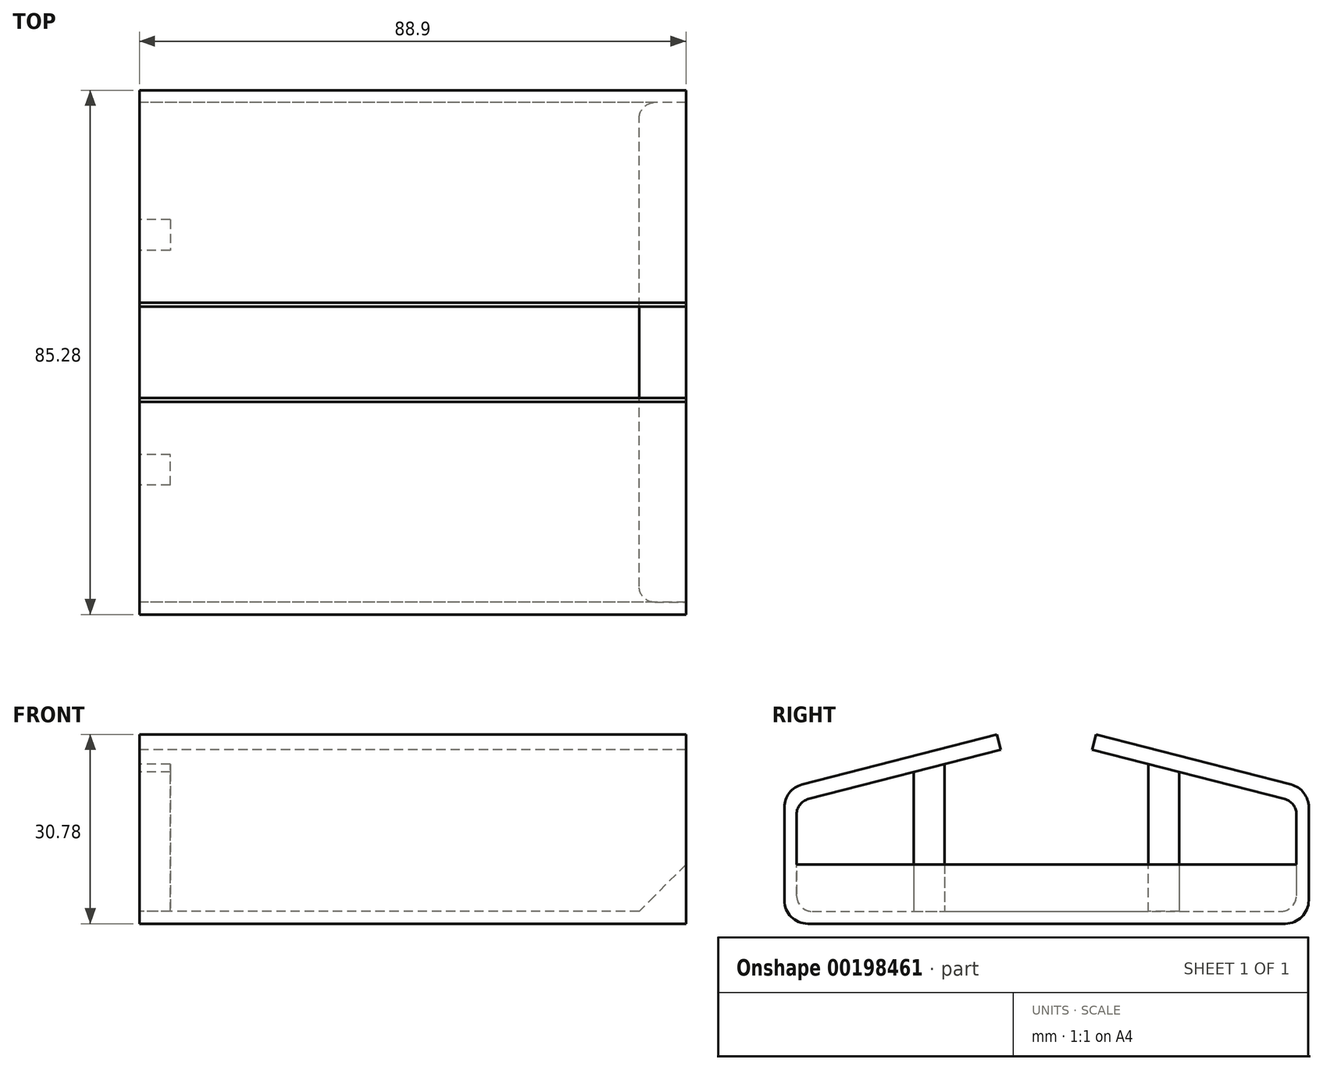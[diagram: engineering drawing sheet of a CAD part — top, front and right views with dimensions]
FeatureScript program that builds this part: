
annotation { "Feature Type Name" : "Feature", "Feature Type Description" : "" }
export const myFeature = defineFeature(function(context is Context, id is Id, definition is map)
    precondition{}
    {
        {
            var Q0;
            Q0=qCreatedBy(makeId("Right.planeOp"),FACE);
            var sketch = newSketch(context, id + "F0", { "sketchPlane" : qUnion([Q0])});
            skLineSegment(sketch, "E0.top", {"start": v(-25.4, 0) * mm, "end": v(59.88, 0) * mm});
            skLineSegment(sketch, "E0.left", {"start": v(-25.4, 21.89) * mm, "end": v(-25.4, 0) * mm});
            skLineSegment(sketch, "E0.right", {"start": v(59.88, 21.89) * mm, "end": v(59.88, 0) * mm});
            skLineSegment(sketch, "E1.top", {"start": v(-23.4, 2) * mm, "end": v(57.88, 2) * mm});
            skLineSegment(sketch, "E1.left", {"start": v(-23.4, 19.78) * mm, "end": v(-23.4, 2) * mm});
            skLineSegment(sketch, "E1.right", {"start": v(57.88, 19.78) * mm, "end": v(57.88, 2) * mm});
            skLineSegment(sketch, "E2", {"start": v(59.88, 21.89) * mm, "end": v(25.3, 30.78) * mm});
            skLineSegment(sketch, "E3", {"start": v(25.3, 30.78) * mm, "end": v(24.67, 28.32) * mm});
            skLineSegment(sketch, "E4", {"start": v(24.67, 28.32) * mm, "end": v(57.88, 19.78) * mm});
            skLineSegment(sketch, "E5", {"start": v(17.24, 0) * mm, "end": v(17.24, 27.47) * mm});
            skLineSegment(sketch, "E6.MirrorCS", {"start": v(9.8, 28.32) * mm, "end": v(-23.4, 19.78) * mm});
            skLineSegment(sketch, "E7.MirrorCS", {"start": v(-25.4, 21.89) * mm, "end": v(9.18, 30.78) * mm});
            skLineSegment(sketch, "E8.MirrorCS", {"start": v(9.18, 30.78) * mm, "end": v(9.8, 28.32) * mm});
            skSolve(sketch);
        }
        {
            var Q0;
            {var subQ4=sQuery(id+"F0.wireOp",EDGE,"E0.right");Q0=makeQuery(id+"F0.imprint","IMPRINT",FACE,{"disambiguationData":[TD([[makeQuery(id+"F0.imprint","IMPRINT",EDGE,{"derivedFrom":subQ4}),-1.0]])]});}
            var Q1;
            {var subQ4=sQuery(id+"F0.wireOp",EDGE,"E0.left");Q1=makeQuery(id+"F0.imprint","IMPRINT",FACE,{"disambiguationData":[TD([[makeQuery(id+"F0.imprint","IMPRINT",EDGE,{"derivedFrom":subQ4}),1.0]])]});}
            extrude(context, id + "F1", {"entities" : qUnion([Q0, Q1]), "depth" : 88.9 * mm});
        }
        {
            var Q0;
            Q0=qCreatedBy(makeId("Right.planeOp"),FACE);
            var sketch = newSketch(context, id + "F2", { "sketchPlane" : qUnion([Q0])});
            skLineSegment(sketch, "E9.top", {"start": v(38.83, 2) * mm, "end": v(33.83, 2) * mm});
            skLineSegment(sketch, "E9.left", {"start": v(38.83, 17.7) * mm, "end": v(38.83, 2) * mm});
            skLineSegment(sketch, "E9.right", {"start": v(33.83, 17.7) * mm, "end": v(33.83, 2) * mm});
            skLineSegment(sketch, "E10.top", {"start": v(-4.35, 2) * mm, "end": v(0.65, 2) * mm});
            skLineSegment(sketch, "E10.left", {"start": v(-4.35, 17.7) * mm, "end": v(-4.35, 2) * mm});
            skLineSegment(sketch, "E10.right", {"start": v(0.65, 17.7) * mm, "end": v(0.65, 2) * mm});
            skLineSegment(sketch, "E11", {"start": v(33.83, 17.7) * mm, "end": v(33.83, 25.97) * mm});
            skLineSegment(sketch, "E12", {"start": v(33.83, 25.97) * mm, "end": v(38.83, 24.68) * mm});
            skLineSegment(sketch, "E13", {"start": v(38.83, 24.68) * mm, "end": v(38.83, 17.7) * mm});
            skLineSegment(sketch, "E14", {"start": v(-4.35, 17.7) * mm, "end": v(-4.35, 24.68) * mm});
            skLineSegment(sketch, "E15", {"start": v(-4.35, 24.68) * mm, "end": v(0.65, 25.97) * mm});
            skLineSegment(sketch, "E16", {"start": v(0.65, 25.97) * mm, "end": v(0.65, 17.7) * mm});
            skSolve(sketch);
        }
        {
            var Q0;
            Q0=makeQuery(id+"F2.imprint","IMPRINT",FACE,{"disambiguationData":[TD([[makeQuery(id+"F2.imprint","IMPRINT",EDGE,{"derivedFrom":sQuery(id+"F2.wireOp",EDGE,"E9.top")}),-1.0]])]});
            var Q1;
            Q1=makeQuery(id+"F2.imprint","IMPRINT",FACE,{"disambiguationData":[TD([[makeQuery(id+"F2.imprint","IMPRINT",EDGE,{"derivedFrom":sQuery(id+"F2.wireOp",EDGE,"E10.top")}),1.0]])]});
            extrude(context, id + "F3", {"entities" : qUnion([Q0, Q1]), "operationType" : NewBodyOperationType.ADD, "depth" : 5 * mm});
        }
        {
            var Q0;
            Q0=makeQuery(id+"F1.opExtrude","CAP_FACE",FACE,{"disambiguationData":[OSD([sQuery(id+"F0.wireOp",EDGE,"E0.bottom"),sQuery(id+"F0.wireOp",EDGE,"E0.top"),sQuery(id+"F0.wireOp",EDGE,"E0.left"),sQuery(id+"F0.wireOp",EDGE,"E0.right"),sQuery(id+"F0.wireOp",EDGE,"E1.bottom"),sQuery(id+"F0.wireOp",EDGE,"E1.top"),sQuery(id+"F0.wireOp",EDGE,"E1.left"),sQuery(id+"F0.wireOp",EDGE,"E1.right"),sQuery(id+"F0.wireOp",EDGE,"VNCxQsE4-ggjW-AWgj-t1wQ-hxSFb9EKYlBE"),sQuery(id+"F0.wireOp",EDGE,"HtSPyxZu-fWGi-P5fe-MJVl-6evfZqa4nhsd"),sQuery(id+"F0.wireOp",EDGE,"2e29113e-a7d3-43c2-ac0c-f86af5c7a188.trimOffspring"),sQuery(id+"F0.wireOp",EDGE,"45b3e84c-9842-4fc3-816f-93033749a0b0.trimOffspring")])],"isStart":false});
            var sketch = newSketch(context, id + "F4", { "sketchPlane" : qUnion([Q0])});
            skLineSegment(sketch, "E17.bottom", {"start": v(-23.4, 2) * mm, "end": v(57.88, 2) * mm});
            skLineSegment(sketch, "E17.top", {"start": v(-23.4, 9.62) * mm, "end": v(57.88, 9.62) * mm});
            skLineSegment(sketch, "E17.left", {"start": v(-23.4, 2) * mm, "end": v(-23.4, 9.62) * mm});
            skLineSegment(sketch, "E17.right", {"start": v(57.88, 2) * mm, "end": v(57.88, 9.62) * mm});
            skSolve(sketch);
        }
        {
            var Q0;
            Q0=makeQuery(id+"F4.imprint","IMPRINT",FACE,{"disambiguationData":[TD([[makeQuery(id+"F4.imprint","IMPRINT",EDGE,{"derivedFrom":sQuery(id+"F4.wireOp",EDGE,"E17.bottom")}),1.0]])]});
            extrude(context, id + "F5", {"entities" : qUnion([Q0]), "operationType" : NewBodyOperationType.ADD, "oppositeDirection" : true, "depth" : 7.62 * mm});
        }
        {
            var Q0;
            Q0=makeQuery(id+"F1.opExtrude","SWEPT_EDGE",EDGE,{"disambiguationData":[OSD([sQuery(id+"F0.wireOp",EDGE,"E0.bottom"),sQuery(id+"F0.wireOp",EDGE,"E0.left")])]});
            var Q1;
            Q1=makeQuery(id+"F1.opExtrude","SWEPT_EDGE",EDGE,{"disambiguationData":[OSD([sQuery(id+"F0.wireOp",EDGE,"E0.top"),sQuery(id+"F0.wireOp",EDGE,"E0.left")])]});
            var Q2;
            Q2=makeQuery(id+"F1.opExtrude","SWEPT_EDGE",EDGE,{"disambiguationData":[OSD([sQuery(id+"F0.wireOp",EDGE,"E0.right"),sQuery(id+"F0.wireOp",EDGE,"2e29113e-a7d3-43c2-ac0c-f86af5c7a188.trimOffspring")])]});
            var Q3;
            Q3=makeQuery(id+"F1.opExtrude","SWEPT_EDGE",EDGE,{"disambiguationData":[OSD([sQuery(id+"F0.wireOp",EDGE,"E0.top"),sQuery(id+"F0.wireOp",EDGE,"E0.right")])]});
            fillet(context, id + "F6", {"entities" : qUnion([Q0, Q1, Q2, Q3]), "radius" : 3.8 * mm, "tangentPropagation" : true, "allowEdgeOverflow" : false});
        }
        {
            var Q0;
            Q0=makeQuery(id+"F1.opExtrude","SWEPT_EDGE",EDGE,{"disambiguationData":[OSD([sQuery(id+"F0.wireOp",EDGE,"E1.right"),sQuery(id+"F0.wireOp",EDGE,"45b3e84c-9842-4fc3-816f-93033749a0b0.trimOffspring")])]});
            var Q1;
            Q1=makeQuery(id+"F1.opExtrude","SWEPT_EDGE",EDGE,{"disambiguationData":[OSD([sQuery(id+"F0.wireOp",EDGE,"E1.bottom"),sQuery(id+"F0.wireOp",EDGE,"E1.left")])]});
            var Q2;
            Q2=makeQuery(id+"F1.opExtrude","SWEPT_EDGE",EDGE,{"disambiguationData":[OSD([sQuery(id+"F0.wireOp",EDGE,"E1.top"),sQuery(id+"F0.wireOp",EDGE,"E1.right")])]});
            var Q3;
            Q3=makeQuery(id+"F1.opExtrude","SWEPT_EDGE",EDGE,{"disambiguationData":[OSD([sQuery(id+"F0.wireOp",EDGE,"E1.top"),sQuery(id+"F0.wireOp",EDGE,"E1.left")])]});
            fillet(context, id + "F7", {"entities" : qUnion([Q0, Q1, Q2, Q3]), "radius" : 2.54 * mm, "tangentPropagation" : true, "allowEdgeOverflow" : false});
        }
        {
            var Q0;
            Q0=makeQuery(id+"F5.opExtrude","CAP_EDGE",EDGE,{"disambiguationData":[OSD([sQuery(id+"F4.wireOp",EDGE,"E17.top")])],"isStart":false});
            chamfer(context, id + "F8", {"entities" : qUnion([Q0]), "width" : 7.62 * mm, "tangentPropagation" : true});
        }
    });
